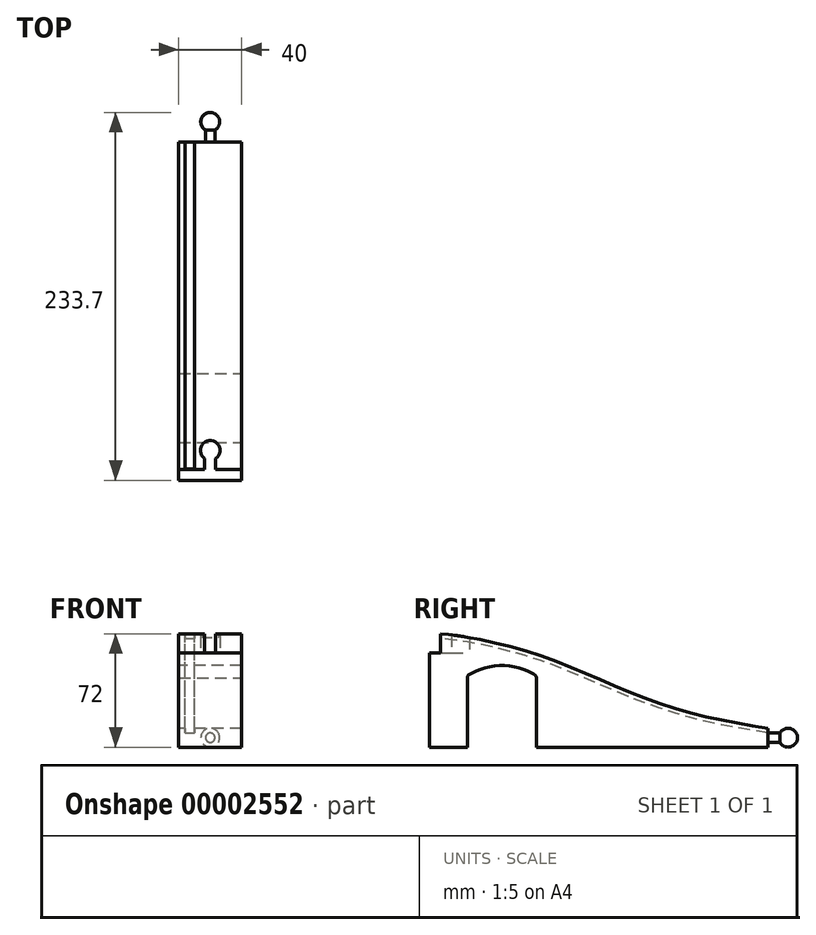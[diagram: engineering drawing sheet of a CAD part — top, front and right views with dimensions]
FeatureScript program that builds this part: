
annotation { "Feature Type Name" : "Feature", "Feature Type Description" : "" }
export const myFeature = defineFeature(function(context is Context, id is Id, definition is map)
    precondition{}
    {
        {
            var Q0;
            Q0=qCreatedBy(makeId("Front.planeOp"),FACE);
            var sketch = newSketch(context, id + "F0", { "sketchPlane" : qUnion([Q0])});
            skLineSegment(sketch, "E0.bottom", {"start": v(0, 0) * mm, "end": v(40, 0) * mm});
            skLineSegment(sketch, "E0.top", {"start": v(0, 12) * mm, "end": v(40, 12) * mm});
            skLineSegment(sketch, "E0.left", {"start": v(0, 0) * mm, "end": v(0, 12) * mm});
            skLineSegment(sketch, "E0.right", {"start": v(40, 0) * mm, "end": v(40, 12) * mm});
            skLineSegment(sketch, "E1.bottom", {"start": v(36, 12) * mm, "end": v(30, 12) * mm});
            skLineSegment(sketch, "E1.top", {"start": v(36, 9) * mm, "end": v(30, 9) * mm});
            skLineSegment(sketch, "E1.left", {"start": v(36, 12) * mm, "end": v(36, 9) * mm});
            skLineSegment(sketch, "E1.right", {"start": v(30, 12) * mm, "end": v(30, 9) * mm});
            skLineSegment(sketch, "E2", {"start": v(20, 12) * mm, "end": v(20, 0) * mm, "construction": true});
            skLineSegment(sketch, "E3.0.MirrorCS", {"start": v(10, 12) * mm, "end": v(10, 9) * mm});
            skLineSegment(sketch, "E3.1.MirrorCS", {"start": v(4, 9) * mm, "end": v(10, 9) * mm});
            skLineSegment(sketch, "E3.2.MirrorCS", {"start": v(4, 12) * mm, "end": v(4, 9) * mm});
            skSolve(sketch);
        }
        {
            var Q0;
            Q0=qCreatedBy(makeId("Right.planeOp"),FACE);
            var sketch = newSketch(context, id + "F1", { "sketchPlane" : qUnion([Q0])});
            skLineSegment(sketch, "E4", {"start": v(0, 0) * mm, "end": v(-215, 0) * mm});
            skLineSegment(sketch, "E5", {"start": v(-215, 0) * mm, "end": v(-215, 60) * mm});
            skLineSegment(sketch, "E6", {"start": v(-215, 60) * mm, "end": v(-208, 60) * mm});
            skLineSegment(sketch, "E7", {"start": v(-208, 60) * mm, "end": v(-208, 72) * mm});
            skLineSegment(sketch, "E8", {"start": v(0, 0) * mm, "end": v(0, 12) * mm});
            skPoint(sketch, "E9", {"position": v(-100, 40) * mm});
            skLineSegment(sketch, "E10", {"start": v(-100, 40) * mm, "end": v(-100, 0) * mm, "construction": true});
            skPoint(sketch, "E11", {"position": v(-50, 22) * mm});
            skLineSegment(sketch, "E12", {"start": v(-50, 22) * mm, "end": v(-50, 0) * mm, "construction": true});
            skPoint(sketch, "E13", {"position": v(-147, 59) * mm});
            skLineSegment(sketch, "E14", {"start": v(-147, 59) * mm, "end": v(-147, 0) * mm, "construction": true});
            skLineSegment(sketch, "E15", {"start": v(-192, 0) * mm, "end": v(-192, 70) * mm, "construction": true});
            skFitSpline(sketch, "E16", {"points": [v(0, 12) * mm, v(-50, 22) * mm, v(-100, 40) * mm, v(-147, 59) * mm, v(-192, 70) * mm, v(-208, 72) * mm], "startDerivative": vector(-226.76, 37.06) * mm, "endDerivative": vector(-111.68, 10.58) * mm});
            skSolve(sketch);
        }
        {
            var Q0;
            Q0=makeQuery(id+"F1.imprint","IMPRINT",FACE,{"disambiguationData":[TD([[makeQuery(id+"F1.imprint","IMPRINT",EDGE,{"derivedFrom":sQuery(id+"F1.wireOp",EDGE,"E4")}),-1.0]])]});
            extrude(context, id + "F2", {"entities" : qUnion([Q0]), "depth" : 40 * mm});
        }
        {
            var Q0;
            Q0=makeQuery(id+"F0.imprint","IMPRINT",FACE,{"disambiguationData":[TD([[makeQuery(id+"F0.imprint","IMPRINT",EDGE,{"derivedFrom":sQuery(id+"F0.wireOp",EDGE,"E1.bottom")}),1.0]])]});
            var Q1;
            {var subQ1=sQuery(id+"F0.wireOp",EDGE,"E3.2.MirrorCS");Q1=makeQuery(id+"F0.imprint","IMPRINT",FACE,{"disambiguationData":[TD([[makeQuery(id+"F0.imprint","IMPRINT",EDGE,{"derivedFrom":subQ1}),1.0]])]});}
            var Q2;
            Q2=sQuery(id+"F1.wireOp",EDGE,"E16");
            sweep(context, id + "F3", {"operationType" : NewBodyOperationType.REMOVE, "profiles" : qUnion([Q0, Q1]), "path" : qUnion([Q2])});
        }
        {
            var Q0;
            Q0=makeQuery(id+"F2.opExtrude","CAP_FACE",FACE,{"disambiguationData":[OSD([sQuery(id+"F1.wireOp",EDGE,"E4"),sQuery(id+"F1.wireOp",EDGE,"E5"),sQuery(id+"F1.wireOp",EDGE,"E6"),sQuery(id+"F1.wireOp",EDGE,"E7"),sQuery(id+"F1.wireOp",EDGE,"E8"),sQuery(id+"F1.wireOp",EDGE,"E16")])],"isStart":false});
            var sketch = newSketch(context, id + "F4", { "sketchPlane" : qUnion([Q0])});
            skLineSegment(sketch, "E17.bottom", {"start": v(-191, 0) * mm, "end": v(-147, 0) * mm});
            skLineSegment(sketch, "E17.top", {"start": v(-191, 44) * mm, "end": v(-147, 44) * mm, "construction": true});
            skLineSegment(sketch, "E17.left", {"start": v(-191, 0) * mm, "end": v(-191, 44) * mm});
            skLineSegment(sketch, "E17.right", {"start": v(-147, 0) * mm, "end": v(-147, 44) * mm});
            skLineSegment(sketch, "E18", {"start": v(-169, 0) * mm, "end": v(-169, 52) * mm, "construction": true});
            skPoint(sketch, "E19", {"position": v(-190.75, 45) * mm});
            skPoint(sketch, "E20.0.MirrorP", {"position": v(-147.25, 45) * mm});
            skFitSpline(sketch, "E21", {"points": [v(-191, 44) * mm, v(-190.75, 45) * mm, v(-169, 52) * mm, v(-147.25, 45) * mm, v(-147, 44) * mm], "startDerivative": vector(5.6, 7.85) * mm, "endDerivative": vector(5.6, -7.85) * mm});
            skSolve(sketch);
        }
        {
            var Q0;
            Q0=makeQuery(id+"F4.imprint","IMPRINT",FACE,{"disambiguationData":[TD([[makeQuery(id+"F4.imprint","IMPRINT",EDGE,{"derivedFrom":sQuery(id+"F4.wireOp",EDGE,"E17.bottom")}),-1.0]])]});
            extrude(context, id + "F5", {"entities" : qUnion([Q0]), "operationType" : NewBodyOperationType.REMOVE, "endBound" : BoundingType.UP_TO_NEXT, "oppositeDirection" : true, "depth" : 25 * mm});
        }
        {
            var Q0;
            Q0=makeQuery(id+"F2.opExtrude","SWEPT_FACE",FACE,{"disambiguationData":[OSD([sQuery(id+"F1.wireOp",EDGE,"E6")])]});
            var sketch = newSketch(context, id + "F6", { "sketchPlane" : qUnion([Q0])});
            skLineSegment(sketch, "E22.rect.left", {"start": v(16.5, -208) * mm, "end": v(16.5, -201.18) * mm});
            skLineSegment(sketch, "E22.rect.right", {"start": v(23.5, -208) * mm, "end": v(23.5, -201.18) * mm});
            skPoint(sketch, "E22.rect.middle", {"position": v(20, -208) * mm});
            skArc(sketch, "E23", {"start": v(23.5, -201.18) * mm, "mid": v(20, -189.75) * mm, "end": v(16.5, -201.18) * mm});
            skLineSegment(sketch, "E24", {"start": v(16.5, -208) * mm, "end": v(23.5, -208) * mm});
            skSolve(sketch);
        }
        {
            var Q0;
            Q0=makeQuery(id+"F6.imprint","IMPRINT",FACE,{"disambiguationData":[TD([[makeQuery(id+"F6.imprint","IMPRINT",EDGE,{"derivedFrom":sQuery(id+"F6.wireOp",EDGE,"E22.rect.left")}),-1.0]])]});
            extrude(context, id + "F7", {"entities" : qUnion([Q0]), "operationType" : NewBodyOperationType.REMOVE, "endBound" : BoundingType.UP_TO_NEXT, "depth" : 25 * mm});
        }
        {
            var Q0;
            {var subQ0=sQuery(id+"F1.wireOp",EDGE,"E4");var subQ1=sQuery(id+"F1.wireOp",EDGE,"E8");Q0=makeQuery(id+"F5.boolean.opBoolean","SPLIT",FACE,{"disambiguationData":[TD([makeQuery(id+"F2.opExtrude","SWEPT_FACE",FACE,{"disambiguationData":[OSD([subQ1])]})])],"derivedFrom":makeQuery(id+"F2.opExtrude","SWEPT_FACE",FACE,{"disambiguationData":[OSD([subQ0])]})});}
            cPlane(context, id + "F8", {"entities" : qUnion([Q0]), "cplaneType" : CPlaneType.OFFSET, "offset" : 6 * mm, "oppositeDirection" : true, "width" : 150 * mm, "height" : 150 * mm});
        }
        {
            var Q0;
            Q0=qCreatedBy(id+"F8.planeOp",FACE);
            var sketch = newSketch(context, id + "F9", { "sketchPlane" : qUnion([Q0])});
            skLineSegment(sketch, "E25", {"start": v(17, 0) * mm, "end": v(17, -7.5) * mm});
            skArc(sketch, "E26", {"start": v(17, -7.5) * mm, "mid": v(14.2, -14.25) * mm, "end": v(20, -18.7) * mm});
            skPoint(sketch, "E27", {"position": v(20, 0) * mm});
            skLineSegment(sketch, "E28", {"start": v(20, 0) * mm, "end": v(20, -18.7) * mm});
            skLineSegment(sketch, "E29", {"start": v(20, 0) * mm, "end": v(17, 0) * mm});
            skSolve(sketch);
        }
        {
            var Q0;
            Q0=makeQuery(id+"F9.imprint","IMPRINT",FACE,{"disambiguationData":[TD([[makeQuery(id+"F9.imprint","IMPRINT",EDGE,{"derivedFrom":sQuery(id+"F9.wireOp",EDGE,"E25")}),1.0]])]});
            var Q1;
            Q1=sQuery(id+"F9.wireOp",EDGE,"E28");
            revolve(context, id + "F10", {"operationType" : NewBodyOperationType.ADD, "entities" : qUnion([Q0]), "axis" : qUnion([Q1]), "revolveType" : RevolveType.FULL});
        }
    });
